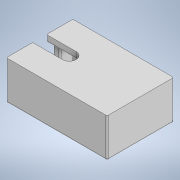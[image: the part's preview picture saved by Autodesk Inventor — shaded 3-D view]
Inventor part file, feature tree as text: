
AUTODESK INVENTOR PART (.ipt)
format: ipt  version: 2021 (Build 250183000, 183)  size: 161,792 bytes
history: native  units: mm
features: extrude x2, sketch x2, other x1, fillet x1, projected_geometry x1
ambient origin geometry x8: Origin, YZ Plane, XZ Plane, XY Plane, X Axis, Y Axis, Z Axis, Center Point
bodies: Body1 (feature_tree)
feature tree (7):
  other  "實體1"
  extrude  "擠出1"  Depth=153.0mm
  extrude  "擠出2"  Depth=101.0mm
  fillet  "圓角1"  Radius=45.0mm
  sketch  "草圖1"
  sketch  "草圖2"
  projected_geometry  "投影迴路1"
